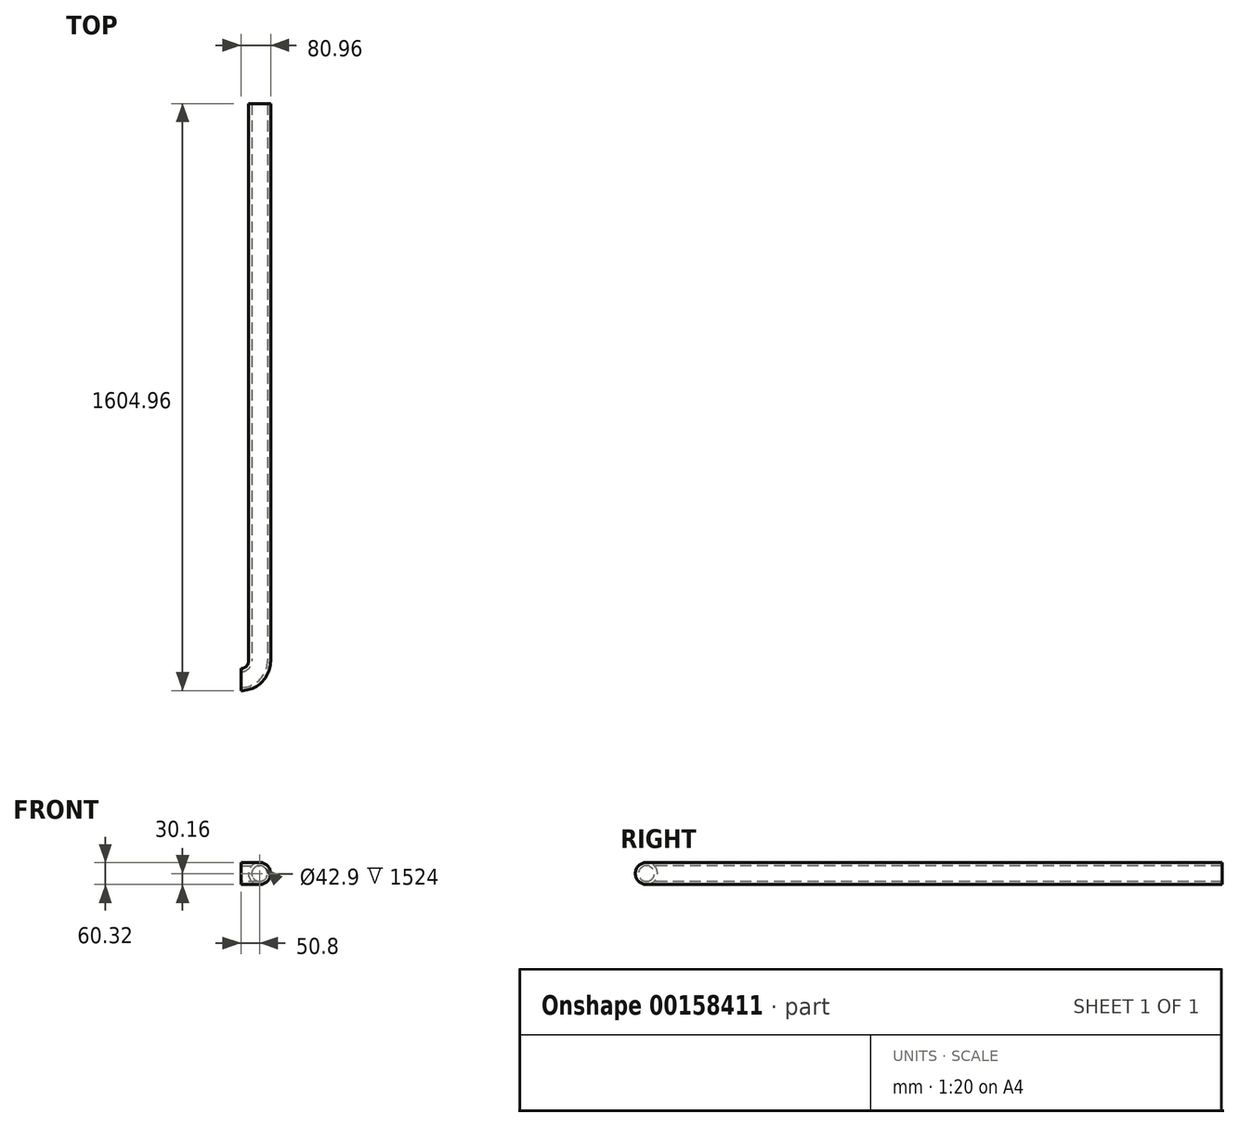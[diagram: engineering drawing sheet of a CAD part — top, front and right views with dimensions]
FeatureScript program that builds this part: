
annotation { "Feature Type Name" : "Feature", "Feature Type Description" : "" }
export const myFeature = defineFeature(function(context is Context, id is Id, definition is map)
    precondition{}
    {
        {
            var Q0;
            Q0=qCreatedBy(makeId("Front.planeOp"),FACE);
            var sketch = newSketch(context, id + "F0", { "sketchPlane" : qUnion([Q0])});
            skCircle(sketch, "E0", {"center": v(0, 0) * mm, "radius": 30.16 * mm});
            skCircle(sketch, "E1.0", {"center": v(0, 0) * mm, "radius": 21.45 * mm});
            skSolve(sketch);
        }
        {
            var Q0;
            Q0=qCreatedBy(makeId("Top.planeOp"),FACE);
            var sketch = newSketch(context, id + "F1", { "sketchPlane" : qUnion([Q0])});
            skLineSegment(sketch, "E2", {"start": v(0, 0) * mm, "end": v(0, -1524) * mm});
            skLineSegment(sketch, "E3", {"start": v(0, -1524) * mm, "end": v(-50.8, -1524) * mm, "construction": true});
            skArc(sketch, "E4", {"start": v(0, -1524) * mm, "mid": v(-14.88, -1559.92) * mm, "end": v(-50.8, -1574.8) * mm});
            skSolve(sketch);
        }
        {
            var Q0;
            Q0=makeQuery(id+"F0.imprint","IMPRINT",FACE,{"disambiguationData":[TD([[makeQuery(id+"F0.imprint","IMPRINT",EDGE,{"derivedFrom":sQuery(id+"F0.wireOp",EDGE,"E0")}),1.0]])]});
            var Q1;
            Q1=sQuery(id+"F1.wireOp",EDGE,"E2");
            var Q2;
            Q2=sQuery(id+"F1.wireOp",EDGE,"E4");
            sweep(context, id + "F2", {"profiles" : qUnion([Q0]), "path" : qUnion([Q1, Q2])});
        }
    });
